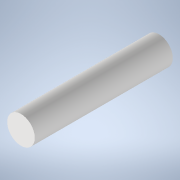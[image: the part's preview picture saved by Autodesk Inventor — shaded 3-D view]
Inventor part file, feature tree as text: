
AUTODESK INVENTOR PART (.ipt)
format: ipt  version: 2022 (Build 260153000, 153)  size: 92,672 bytes
history: native  units: mm
features: extrude x1, sketch x1
ambient origin geometry x8: Origin, YZ Plane, XZ Plane, XY Plane, X Axis, Y Axis, Z Axis, Center Point
bodies: Volumenkörper1 (feature_tree)
feature tree (2):
  extrude  "Extrusion1"  Depth=10.0mm TaperAngle=0.0deg
  sketch  "Skizze1"  dims[d0=2.0mm d1=10.0mm d2=0.0mm]
